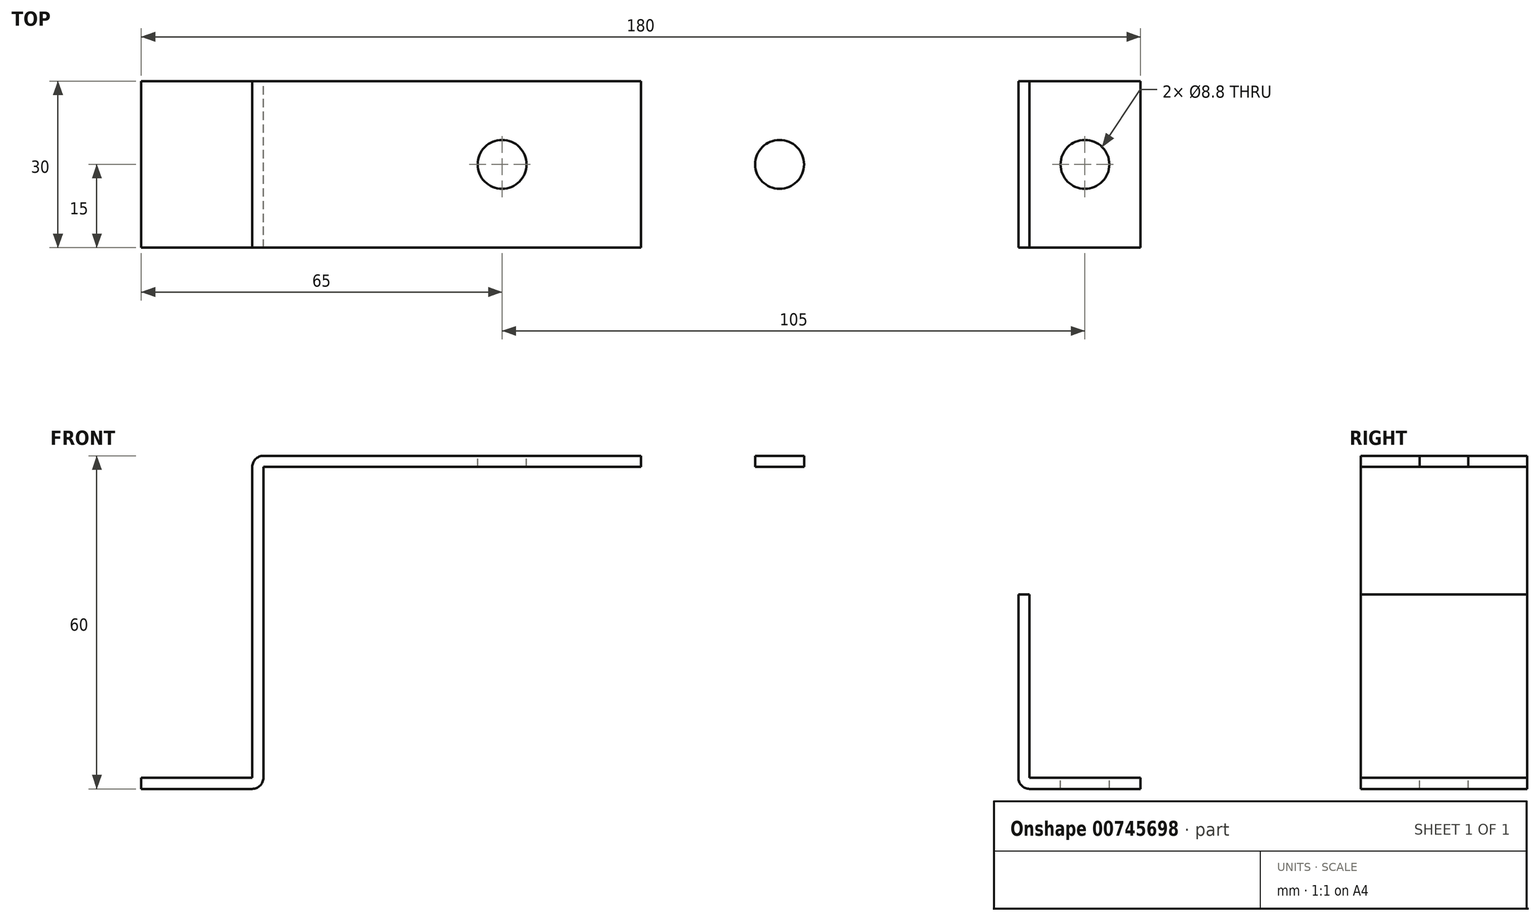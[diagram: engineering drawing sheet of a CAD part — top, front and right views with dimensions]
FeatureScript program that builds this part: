
annotation { "Feature Type Name" : "Feature", "Feature Type Description" : "" }
export const myFeature = defineFeature(function(context is Context, id is Id, definition is map)
    precondition{}
    {
        {
            var Q0;
            Q0=qCreatedBy(makeId("Front.planeOp"),FACE);
            var sketch = newSketch(context, id + "F0", { "sketchPlane" : qUnion([Q0])});
            skLineSegment(sketch, "E0.bottom", {"start": v(90, 1) * mm, "end": v(70, 1) * mm});
            skLineSegment(sketch, "E0.top", {"start": v(90, -1) * mm, "end": v(68, -1) * mm});
            skLineSegment(sketch, "E0.left", {"start": v(90, 1) * mm, "end": v(90, -1) * mm});
            skLineSegment(sketch, "E0.right", {"start": v(-90, 1) * mm, "end": v(-90, -1) * mm});
            skPoint(sketch, "E0.middle", {"position": v(0, 0) * mm});
            skLineSegment(sketch, "E1.top", {"start": v(-70, 59) * mm, "end": v(70, 59) * mm});
            skLineSegment(sketch, "E1.left", {"start": v(-70, 1) * mm, "end": v(-70, 59) * mm});
            skLineSegment(sketch, "E1.right", {"start": v(70, 1) * mm, "end": v(70, 59) * mm});
            skLineSegment(sketch, "E2.0", {"start": v(-68, 57) * mm, "end": v(68, 57) * mm});
            skLineSegment(sketch, "E3.0", {"start": v(-68, -1) * mm, "end": v(-68, 57) * mm});
            skLineSegment(sketch, "E4.0", {"start": v(68, -1) * mm, "end": v(68, 57) * mm});
            skLineSegment(sketch, "E5.trimOffspring", {"start": v(-68, -1) * mm, "end": v(-90, -1) * mm});
            skLineSegment(sketch, "E6.trimOffspring", {"start": v(-70, 1) * mm, "end": v(-90, 1) * mm});
            skPoint(sketch, "E7.orphan", {"position": v(0, 1) * mm});
            skSolve(sketch);
        }
        {
            var Q0;
            Q0=makeQuery(id+"F0.imprint","IMPRINT",FACE,{"disambiguationData":[TD([[makeQuery(id+"F0.imprint","IMPRINT",EDGE,{"derivedFrom":sQuery(id+"F0.wireOp",EDGE,"E0.bottom")}),1.0]])]});
            extrude(context, id + "F1", {"entities" : qUnion([Q0]), "depth" : 30 * mm, "offsetDistance" : 25 * mm});
        }
        {
            var Q0;
            Q0=makeQuery(id+"F1.opExtrude","SWEPT_FACE",FACE,{"disambiguationData":[OSD([sQuery(id+"F0.wireOp",EDGE,"E0.bottom")])]});
            var sketch = newSketch(context, id + "F2", { "sketchPlane" : qUnion([Q0])});
            skCircle(sketch, "E8", {"center": v(80, -15) * mm, "radius": 4.4 * mm});
            skCircle(sketch, "E9.MirrorC", {"center": v(-80, -15) * mm, "radius": 4.4 * mm});
            skSolve(sketch);
        }
        {
            var Q0;
            Q0=makeQuery(id+"F1.opExtrude","SWEPT_FACE",FACE,{"disambiguationData":[OSD([sQuery(id+"F0.wireOp",EDGE,"E1.top")])]});
            var sketch = newSketch(context, id + "F3", { "sketchPlane" : qUnion([Q0])});
            skLineSegment(sketch, "E10", {"start": v(0, 0) * mm, "end": v(0, -30) * mm});
            skCircle(sketch, "E11", {"center": v(-25, -15) * mm, "radius": 4.4 * mm});
            skCircle(sketch, "E12.MirrorC", {"center": v(25, -15) * mm, "radius": 4.4 * mm});
            skSolve(sketch);
        }
        {
            var Q0;
            Q0=makeQuery(id+"F2.imprint","IMPRINT",FACE,{"disambiguationData":[TD([[makeQuery(id+"F2.imprint","IMPRINT",EDGE,{"derivedFrom":sQuery(id+"F2.wireOp",EDGE,"E9.MirrorC")}),-1.0]])]});
            var Q1;
            Q1=makeQuery(id+"F3.imprint","IMPRINT",FACE,{"disambiguationData":[TD([[makeQuery(id+"F3.imprint","IMPRINT",EDGE,{"derivedFrom":sQuery(id+"F3.wireOp",EDGE,"E11")}),1.0]])]});
            var Q2;
            Q2=makeQuery(id+"F3.imprint","IMPRINT",FACE,{"disambiguationData":[TD([[makeQuery(id+"F3.imprint","IMPRINT",EDGE,{"derivedFrom":sQuery(id+"F3.wireOp",EDGE,"E12.MirrorC")}),-1.0]])]});
            var Q3;
            {var subQ0=sQuery(id+"F2.wireOp",EDGE,"E8");var subQ1=sQuery(id+"F2.wireOp",EDGE,"qyHaVNaX-OBYY-w3NK-5kQH-MvDpQNjSdSPX");var subQ2=makeQuery(id+"F2.imprint","INTERSECT",VERTEX,{"disambiguationData":[OD(0.0)],"derivedFrom":[subQ1,subQ0]});Q3=makeQuery(id+"F2.imprint","IMPRINT",FACE,{"disambiguationData":[TD([[makeQuery(id+"F2.imprint","IMPRINT",EDGE,{"disambiguationData":[TD([[subQ2,-1.0]])],"derivedFrom":subQ1}),-1.0]])]});}
            var Q4;
            {var subQ0=sQuery(id+"F2.wireOp",EDGE,"E8");var subQ1=sQuery(id+"F2.wireOp",EDGE,"qyHaVNaX-OBYY-w3NK-5kQH-MvDpQNjSdSPX");var subQ2=makeQuery(id+"F2.imprint","INTERSECT",VERTEX,{"disambiguationData":[OD(0.0)],"derivedFrom":[subQ1,subQ0]});Q4=makeQuery(id+"F2.imprint","IMPRINT",FACE,{"disambiguationData":[TD([[makeQuery(id+"F2.imprint","IMPRINT",EDGE,{"disambiguationData":[TD([[subQ2,-1.0]])],"derivedFrom":subQ1}),1.0]])]});}
            var Q5;
            Q5=makeQuery(id+"F2.imprint","IMPRINT",FACE,{"disambiguationData":[TD([[makeQuery(id+"F2.imprint","IMPRINT",EDGE,{"derivedFrom":sQuery(id+"F2.wireOp",EDGE,"E8")}),1.0]])]});
            extrude(context, id + "F4", {"entities" : qUnion([Q0, Q1, Q2, Q3, Q4, Q5]), "operationType" : NewBodyOperationType.REMOVE, "oppositeDirection" : true, "depth" : 25 * mm, "offsetDistance" : 25 * mm});
        }
        {
            var Q0;
            Q0=makeQuery(id+"F1.opExtrude","SWEPT_EDGE",EDGE,{"disambiguationData":[OSD([sQuery(id+"F0.wireOp",EDGE,"E1.top"),sQuery(id+"F0.wireOp",EDGE,"E1.left")])]});
            var Q1;
            Q1=makeQuery(id+"F1.opExtrude","SWEPT_EDGE",EDGE,{"disambiguationData":[OSD([sQuery(id+"F0.wireOp",EDGE,"E1.top"),sQuery(id+"F0.wireOp",EDGE,"E1.right")])]});
            fillet(context, id + "F5", {"entities" : qUnion([Q0, Q1]), "radius" : 2 * mm, "tangentPropagation" : true, "allowEdgeOverflow" : false});
        }
        {
            var Q0;
            Q0=makeQuery(id+"F1.opExtrude","SWEPT_EDGE",EDGE,{"disambiguationData":[OSD([sQuery(id+"F0.wireOp",EDGE,"E0.top"),sQuery(id+"F0.wireOp",EDGE,"E4.0")])]});
            var Q1;
            Q1=makeQuery(id+"F1.opExtrude","SWEPT_EDGE",EDGE,{"disambiguationData":[OSD([sQuery(id+"F0.wireOp",EDGE,"E3.0"),sQuery(id+"F0.wireOp",EDGE,"E5.trimOffspring")])]});
            fillet(context, id + "F6", {"entities" : qUnion([Q0, Q1]), "radius" : 2 * mm, "tangentPropagation" : true, "allowEdgeOverflow" : false});
        }
    });
